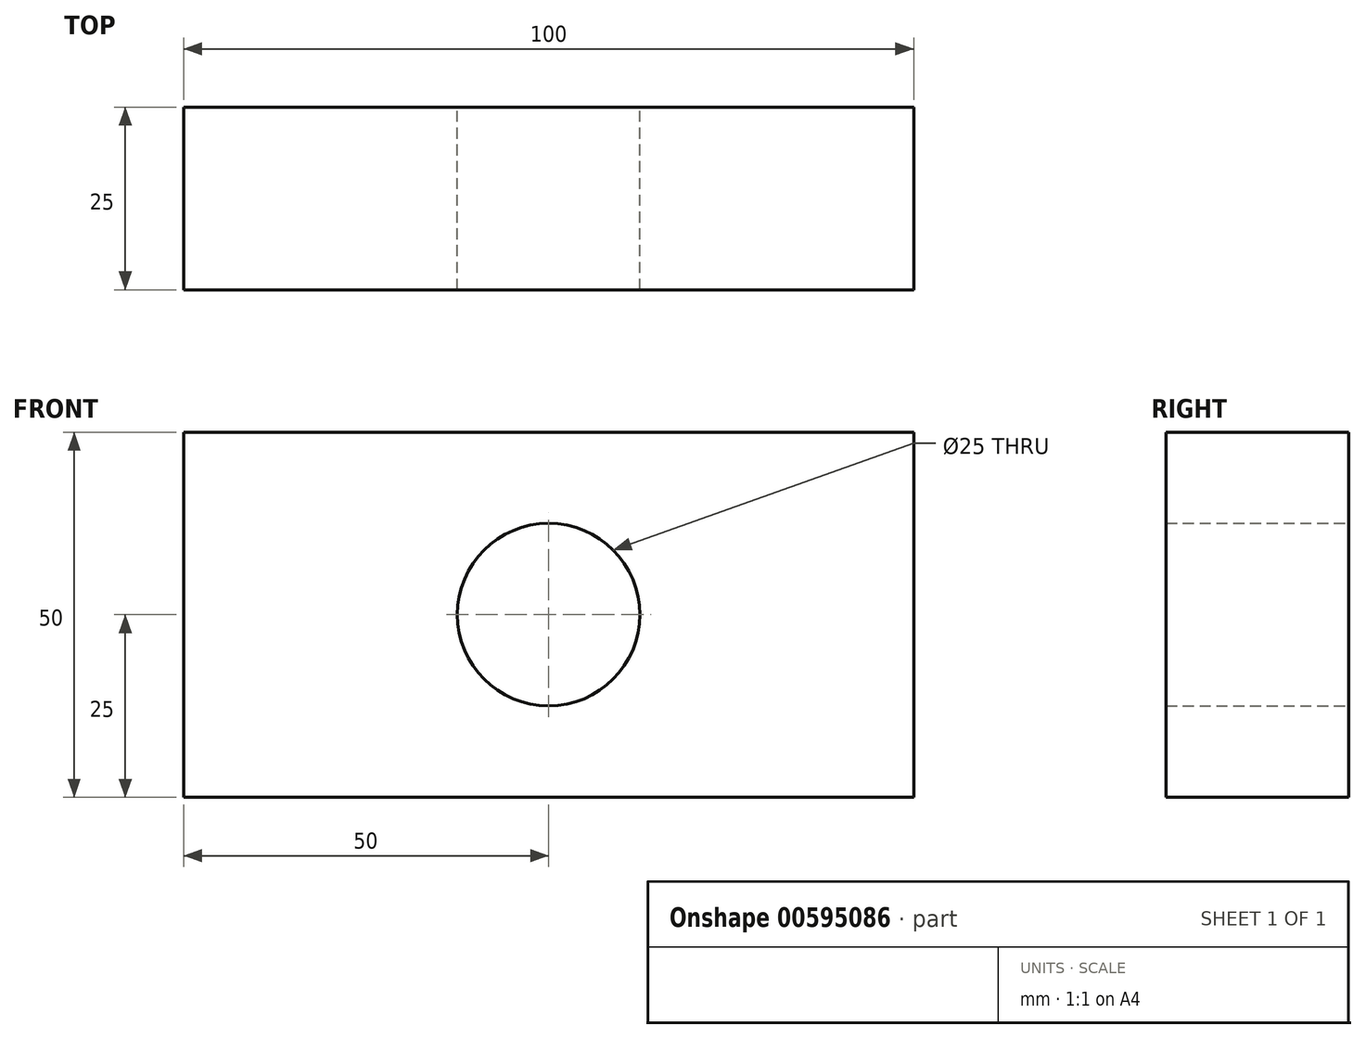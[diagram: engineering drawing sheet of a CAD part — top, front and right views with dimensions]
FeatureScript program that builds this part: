
annotation { "Feature Type Name" : "Feature", "Feature Type Description" : "" }
export const myFeature = defineFeature(function(context is Context, id is Id, definition is map)
    precondition{}
    {
        {
            var Q0;
            Q0=qCreatedBy(makeId("Front.planeOp"),FACE);
            var sketch = newSketch(context, id + "F0", { "sketchPlane" : qUnion([Q0])});
            skLineSegment(sketch, "E0.bottom", {"start": v(50, 25) * mm, "end": v(-50, 25) * mm});
            skLineSegment(sketch, "E0.top", {"start": v(50, -25) * mm, "end": v(-50, -25) * mm});
            skLineSegment(sketch, "E0.left", {"start": v(50, 25) * mm, "end": v(50, -25) * mm});
            skLineSegment(sketch, "E0.right", {"start": v(-50, 25) * mm, "end": v(-50, -25) * mm});
            skPoint(sketch, "E0.middle", {"position": v(0, 0) * mm});
            skCircle(sketch, "E1", {"center": v(0, 0) * mm, "radius": 12.5 * mm});
            skSolve(sketch);
        }
        {
            var Q0;
            Q0=makeQuery(id+"F0.imprint","IMPRINT",FACE,{"disambiguationData":[TD([[makeQuery(id+"F0.imprint","IMPRINT",EDGE,{"derivedFrom":sQuery(id+"F0.wireOp",EDGE,"E0.bottom")}),1.0]])]});
            extrude(context, id + "F1", {"entities" : qUnion([Q0]), "depth" : 25 * mm, "offsetDistance" : 25 * mm});
        }
    });
